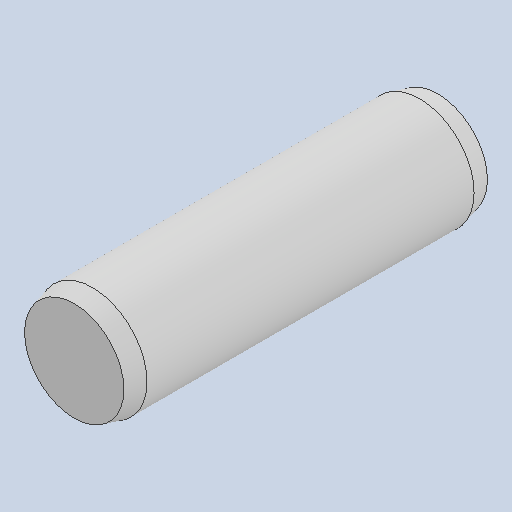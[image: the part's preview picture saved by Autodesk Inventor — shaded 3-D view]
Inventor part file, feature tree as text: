
AUTODESK INVENTOR PART (.ipt)
format: ipt  version: 2025 (Build 290162000, 162)  size: 98,816 bytes
history: native  units: in
note: dims shown in document units (in); Inventor stores cm internally (conversion verified against a paired STEP export)
features: revolve x1
ambient origin geometry x8: Origin, YZ Plane, XZ Plane, XY Plane, X Axis, Y Axis, Z Axis, Center Point
bodies: Solid1 (feature_tree)
feature tree (1):
  revolve  "Revolve1"  [1 undecoded]
note: 1 required parameter value undecoded (feature->parameter linkage not recoverable at this tier; creation-order binding heuristic only, values carry confidence <= 0.55)
